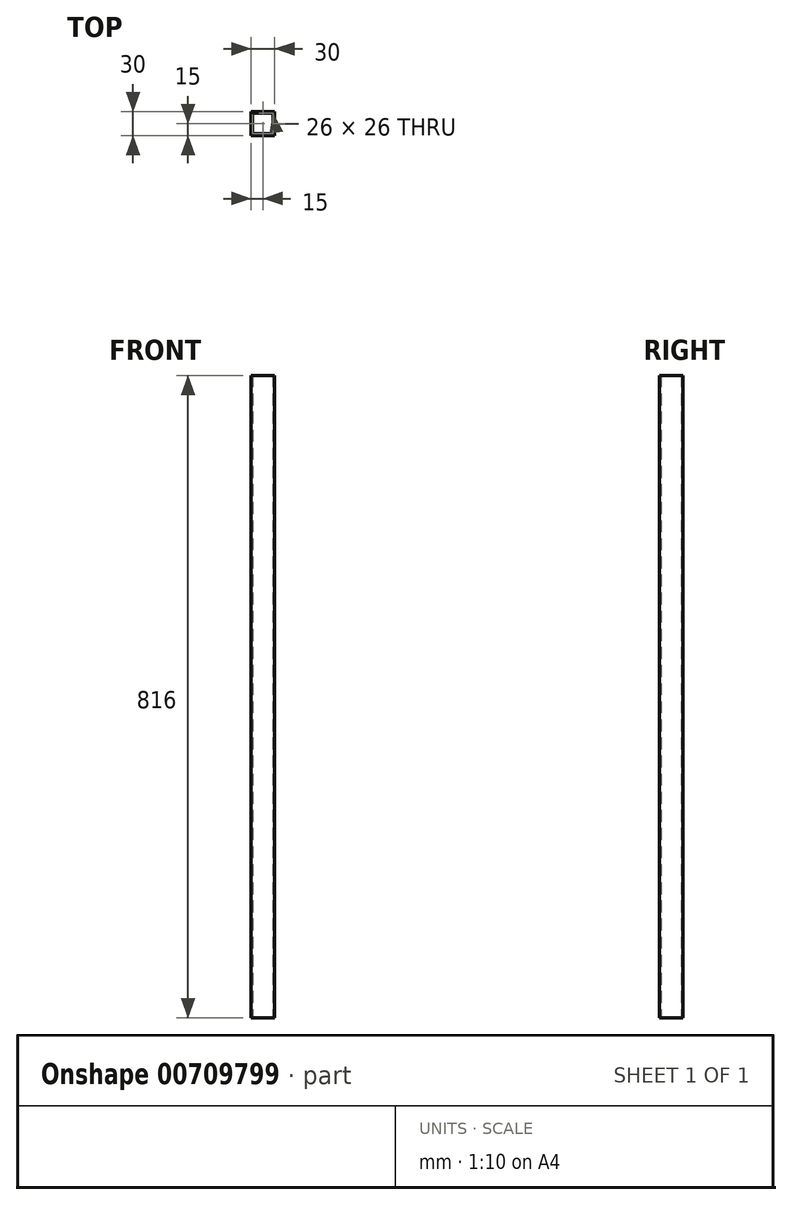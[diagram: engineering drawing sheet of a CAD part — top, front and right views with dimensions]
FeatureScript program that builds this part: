
annotation { "Feature Type Name" : "Feature", "Feature Type Description" : "" }
export const myFeature = defineFeature(function(context is Context, id is Id, definition is map)
    precondition{}
    {
        {
            var Q0;
            Q0=qCreatedBy(makeId("Top.planeOp"),FACE);
            var sketch = newSketch(context, id + "F0", { "sketchPlane" : qUnion([Q0])});
            skLineSegment(sketch, "E0.bottom", {"start": v(0, 0) * mm, "end": v(-30, 0) * mm});
            skLineSegment(sketch, "E0.top", {"start": v(0, 30) * mm, "end": v(-30, 30) * mm});
            skLineSegment(sketch, "E0.left", {"start": v(0, 0) * mm, "end": v(0, 30) * mm});
            skLineSegment(sketch, "E0.right", {"start": v(-30, 0) * mm, "end": v(-30, 30) * mm});
            skLineSegment(sketch, "E1.0", {"start": v(-2, 2) * mm, "end": v(-2, 28) * mm});
            skLineSegment(sketch, "E1.1", {"start": v(-2, 2) * mm, "end": v(-28, 2) * mm});
            skLineSegment(sketch, "E1.2", {"start": v(-28, 2) * mm, "end": v(-28, 28) * mm});
            skLineSegment(sketch, "E1.3", {"start": v(-2, 28) * mm, "end": v(-28, 28) * mm});
            skSolve(sketch);
        }
        {
            var Q0;
            Q0=makeQuery(id+"F0.imprint","IMPRINT",FACE,{"disambiguationData":[TD([[makeQuery(id+"F0.imprint","IMPRINT",EDGE,{"derivedFrom":sQuery(id+"F0.wireOp",EDGE,"E0.bottom")}),-1.0]])]});
            extrude(context, id + "F1", {"entities" : qUnion([Q0]), "depth" : 816 * mm, "offsetDistance" : 25 * mm});
        }
    });
